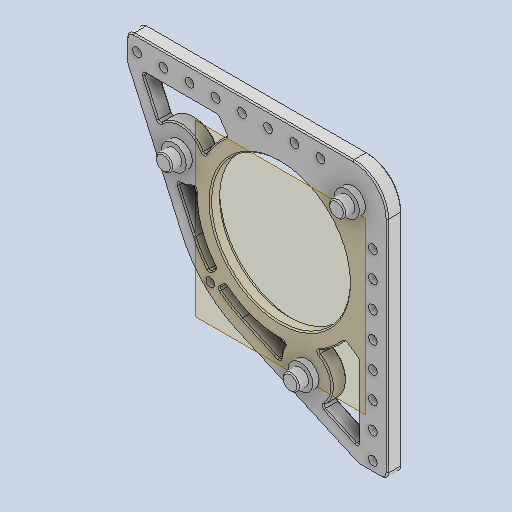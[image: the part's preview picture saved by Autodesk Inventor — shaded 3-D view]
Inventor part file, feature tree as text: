
AUTODESK INVENTOR PART (.ipt)
format: ipt  version: 2022 (Build 260153000, 153)  size: 403,968 bytes
history: native  units: in
note: dims shown in document units (in); Inventor stores cm internally (conversion verified against a paired STEP export)
features: sketch x4, other x3, plane x1
ambient origin geometry x8: Origin, YZ Plane, XZ Plane, XY Plane, X Axis, Y Axis, Z Axis, Center Point
bodies: Solid1 (feature_tree)
feature tree (8):
  other  "lower_plate.ipt"
  other  "Solid1::lower_plate.ipt"
  other  "TaggingFeature1"
  sketch  "Sketch1"  dims[d0=0.3937in]
  sketch  "Sketch4"
  sketch  "Sketch5"
  sketch  "Sketch6"
  plane  "Work Plane1"
